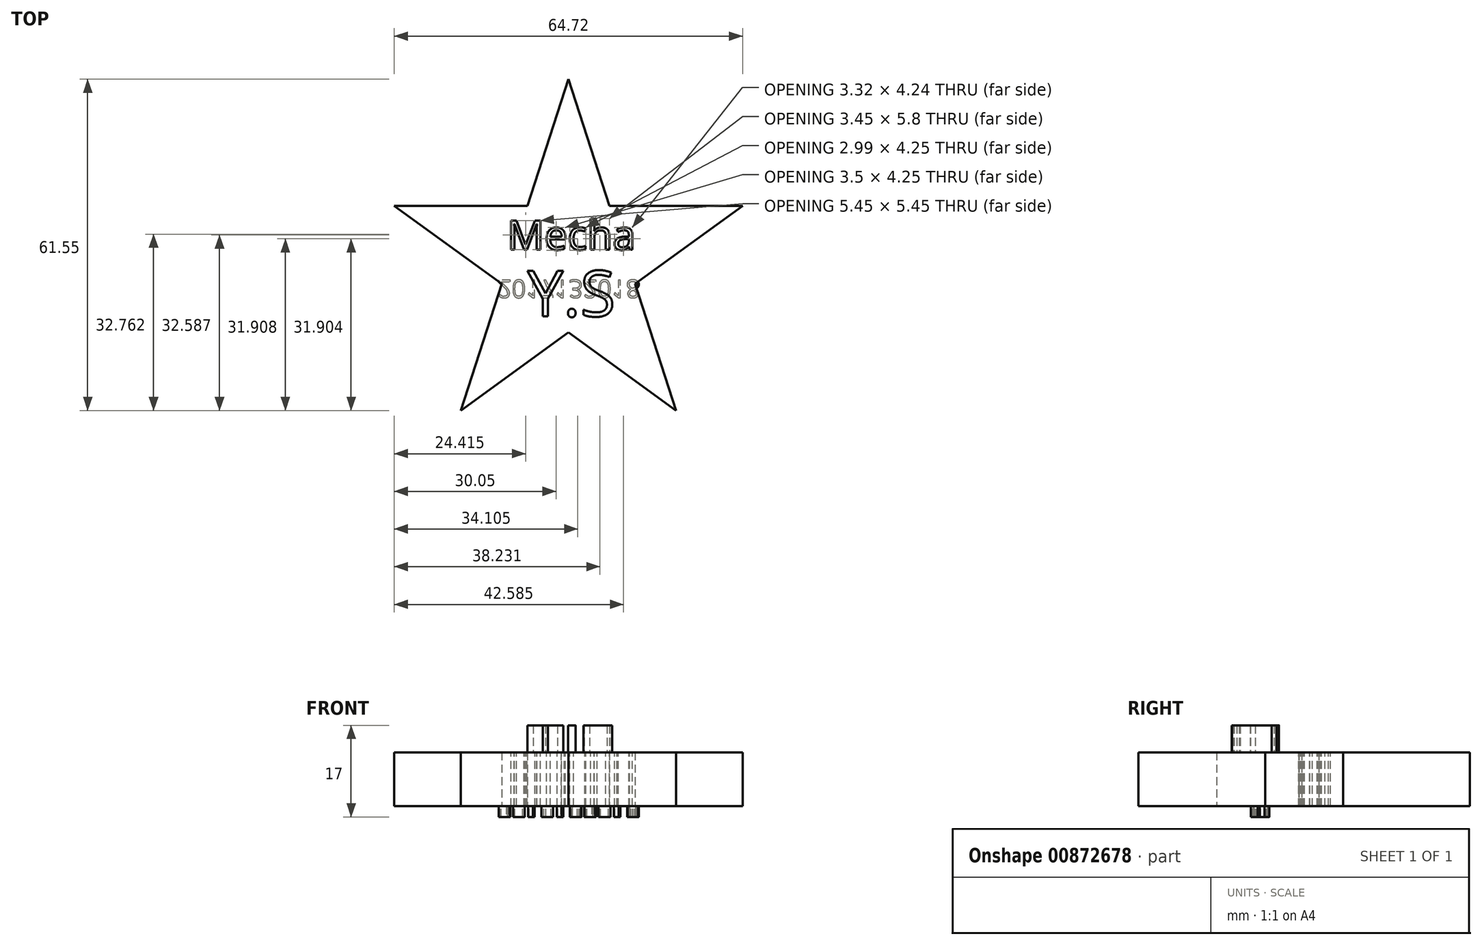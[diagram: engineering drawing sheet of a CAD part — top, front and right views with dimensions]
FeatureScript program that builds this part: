
annotation { "Feature Type Name" : "Feature", "Feature Type Description" : "" }
export const myFeature = defineFeature(function(context is Context, id is Id, definition is map)
    precondition{}
    {
        {
            var Q0;
            Q0=qCreatedBy(makeId("Top.planeOp"),FACE);
            var sketch = newSketch(context, id + "F0", { "sketchPlane" : qUnion([Q0])});
            skLineSegment(sketch, "E0", {"start": v(-32.36, 7.95) * mm, "end": v(-7.64, 7.95) * mm});
            skLineSegment(sketch, "E1", {"start": v(32.36, 7.95) * mm, "end": v(12.36, -6.58) * mm});
            skLineSegment(sketch, "E2", {"start": v(-32.36, 7.95) * mm, "end": v(-12.36, -6.58) * mm});
            skLineSegment(sketch, "E3", {"start": v(0, 31.46) * mm, "end": v(7.64, 7.95) * mm});
            skLineSegment(sketch, "E4", {"start": v(0, 31.46) * mm, "end": v(-7.64, 7.95) * mm});
            skLineSegment(sketch, "E5.trimOffspring", {"start": v(-12.36, -6.58) * mm, "end": v(-20, -30.1) * mm});
            skLineSegment(sketch, "E6.trimOffspring", {"start": v(12.36, -6.58) * mm, "end": v(20, -30.1) * mm});
            skLineSegment(sketch, "E7.trimOffspring", {"start": v(7.64, 7.95) * mm, "end": v(32.36, 7.95) * mm});
            skLineSegment(sketch, "E8.trimOffspring", {"start": v(0, -15.56) * mm, "end": v(20, -30.1) * mm});
            skLineSegment(sketch, "E9.trimOffspring", {"start": v(0, -15.56) * mm, "end": v(-20, -30.1) * mm});
            skSolve(sketch);
        }
        {
            var Q0;
            Q0=makeQuery(id+"F0.imprint","IMPRINT",FACE,{"disambiguationData":[TD([[makeQuery(id+"F0.imprint","IMPRINT",EDGE,{"derivedFrom":sQuery(id+"F0.wireOp",EDGE,"E0")}),-1.0]])]});
            extrude(context, id + "F1", {"entities" : qUnion([Q0]), "endBound" : BoundingType.SYMMETRIC, "depth" : 10 * mm, "offsetDistance" : 25 * mm});
        }
        {
            var Q0;
            Q0=makeQuery(id+"F1.opExtrude","CAP_FACE",FACE,{"disambiguationData":[OSD([sQuery(id+"F0.wireOp",EDGE,"E0"),sQuery(id+"F0.wireOp",EDGE,"E1"),sQuery(id+"F0.wireOp",EDGE,"E2"),sQuery(id+"F0.wireOp",EDGE,"E3"),sQuery(id+"F0.wireOp",EDGE,"E4"),sQuery(id+"F0.wireOp",EDGE,"E5.trimOffspring"),sQuery(id+"F0.wireOp",EDGE,"E6.trimOffspring"),sQuery(id+"F0.wireOp",EDGE,"E7.trimOffspring"),sQuery(id+"F0.wireOp",EDGE,"E8.trimOffspring"),sQuery(id+"F0.wireOp",EDGE,"E9.trimOffspring")])],"isStart":false});
            var sketch = newSketch(context, id + "F2", { "sketchPlane" : qUnion([Q0])});
            skText(sketch, "E10", { "text": "Mecha", "fontName": "NotoSans-Regular.ttf"});
            const initialGuessF2  = {"E10": [-0.01141, -0.00023, 1, 0, 0.0055]};
            skSetInitialGuess(sketch, initialGuessF2);
            skSolve(sketch);
        }
        {
            var Q0;
            Q0 = qSketchRegion(id + "F2", true);
            extrude(context, id + "F3", {"entities" : qUnion([Q0]), "operationType" : NewBodyOperationType.REMOVE, "oppositeDirection" : true, "depth" : 10 * mm, "offsetDistance" : 25 * mm});
        }
        {
            var Q0;
            {var subQ0=sQuery(id+"F0.wireOp",EDGE,"E8.trimOffspring");var subQ1=sQuery(id+"F0.wireOp",EDGE,"E7.trimOffspring");var subQ2=sQuery(id+"F0.wireOp",EDGE,"E6.trimOffspring");var subQ3=sQuery(id+"F0.wireOp",EDGE,"E5.trimOffspring");var subQ4=sQuery(id+"F0.wireOp",EDGE,"E4");var subQ5=sQuery(id+"F0.wireOp",EDGE,"E9.trimOffspring");var subQ6=sQuery(id+"F0.wireOp",EDGE,"E0");var subQ7=sQuery(id+"F0.wireOp",EDGE,"E3");var subQ8=sQuery(id+"F0.wireOp",EDGE,"E1");var subQ9=sQuery(id+"F0.wireOp",EDGE,"E2");Q0=makeQuery(id+"F3.boolean.opBoolean","SPLIT",FACE,{"disambiguationData":[TD([makeQuery(id+"F1.opExtrude","SWEPT_FACE",FACE,{"disambiguationData":[OSD([subQ6])]})])],"derivedFrom":makeQuery(id+"F1.opExtrude","CAP_FACE",FACE,{"disambiguationData":[OSD([subQ6,subQ8,subQ9,subQ7,subQ4,subQ3,subQ2,subQ1,subQ0,subQ5])],"isStart":false})});}
            var sketch = newSketch(context, id + "F4", { "sketchPlane" : qUnion([Q0])});
            skText(sketch, "E11", { "text": "Y.S", "fontName": "OpenSans-Regular.ttf"});
            const initialGuessF4  = {"E11": [-0.0076, -0.0126, 1, 0, 0.00855]};
            skSetInitialGuess(sketch, initialGuessF4);
            skSolve(sketch);
        }
        {
            var Q0;
            Q0 = qSketchRegion(id + "F4", true);
            extrude(context, id + "F5", {"entities" : qUnion([Q0]), "operationType" : NewBodyOperationType.ADD, "depth" : 5 * mm, "offsetDistance" : 25 * mm});
        }
        {
            var Q0;
            {var subQ0=sQuery(id+"F0.wireOp",EDGE,"E8.trimOffspring");var subQ1=sQuery(id+"F0.wireOp",EDGE,"E7.trimOffspring");var subQ2=sQuery(id+"F0.wireOp",EDGE,"E6.trimOffspring");var subQ3=sQuery(id+"F0.wireOp",EDGE,"E5.trimOffspring");var subQ4=sQuery(id+"F0.wireOp",EDGE,"E4");var subQ5=sQuery(id+"F0.wireOp",EDGE,"E9.trimOffspring");var subQ6=sQuery(id+"F0.wireOp",EDGE,"E0");var subQ7=sQuery(id+"F0.wireOp",EDGE,"E3");var subQ8=sQuery(id+"F0.wireOp",EDGE,"E1");var subQ9=sQuery(id+"F0.wireOp",EDGE,"E2");Q0=makeQuery(id+"F3.boolean.opBoolean","SPLIT",FACE,{"disambiguationData":[TD([makeQuery(id+"F1.opExtrude","SWEPT_FACE",FACE,{"disambiguationData":[OSD([subQ6])]})])],"derivedFrom":makeQuery(id+"F1.opExtrude","CAP_FACE",FACE,{"disambiguationData":[OSD([subQ6,subQ8,subQ9,subQ7,subQ4,subQ3,subQ2,subQ1,subQ0,subQ5])],"isStart":true})});}
            var sketch = newSketch(context, id + "F6", { "sketchPlane" : qUnion([Q0])});
            skText(sketch, "E12", { "text": "2017132018", "fontName": "OpenSans-Regular.ttf"});
            const initialGuessF6  = {"E12": [-0.0132, 0.00583, 1, 0, 0.00334]};
            skSetInitialGuess(sketch, initialGuessF6);
            skSolve(sketch);
        }
        {
            var Q0;
            Q0 = qSketchRegion(id + "F6", true);
            extrude(context, id + "F7", {"entities" : qUnion([Q0]), "operationType" : NewBodyOperationType.ADD, "depth" : 2 * mm, "offsetDistance" : 25 * mm});
        }
    });
